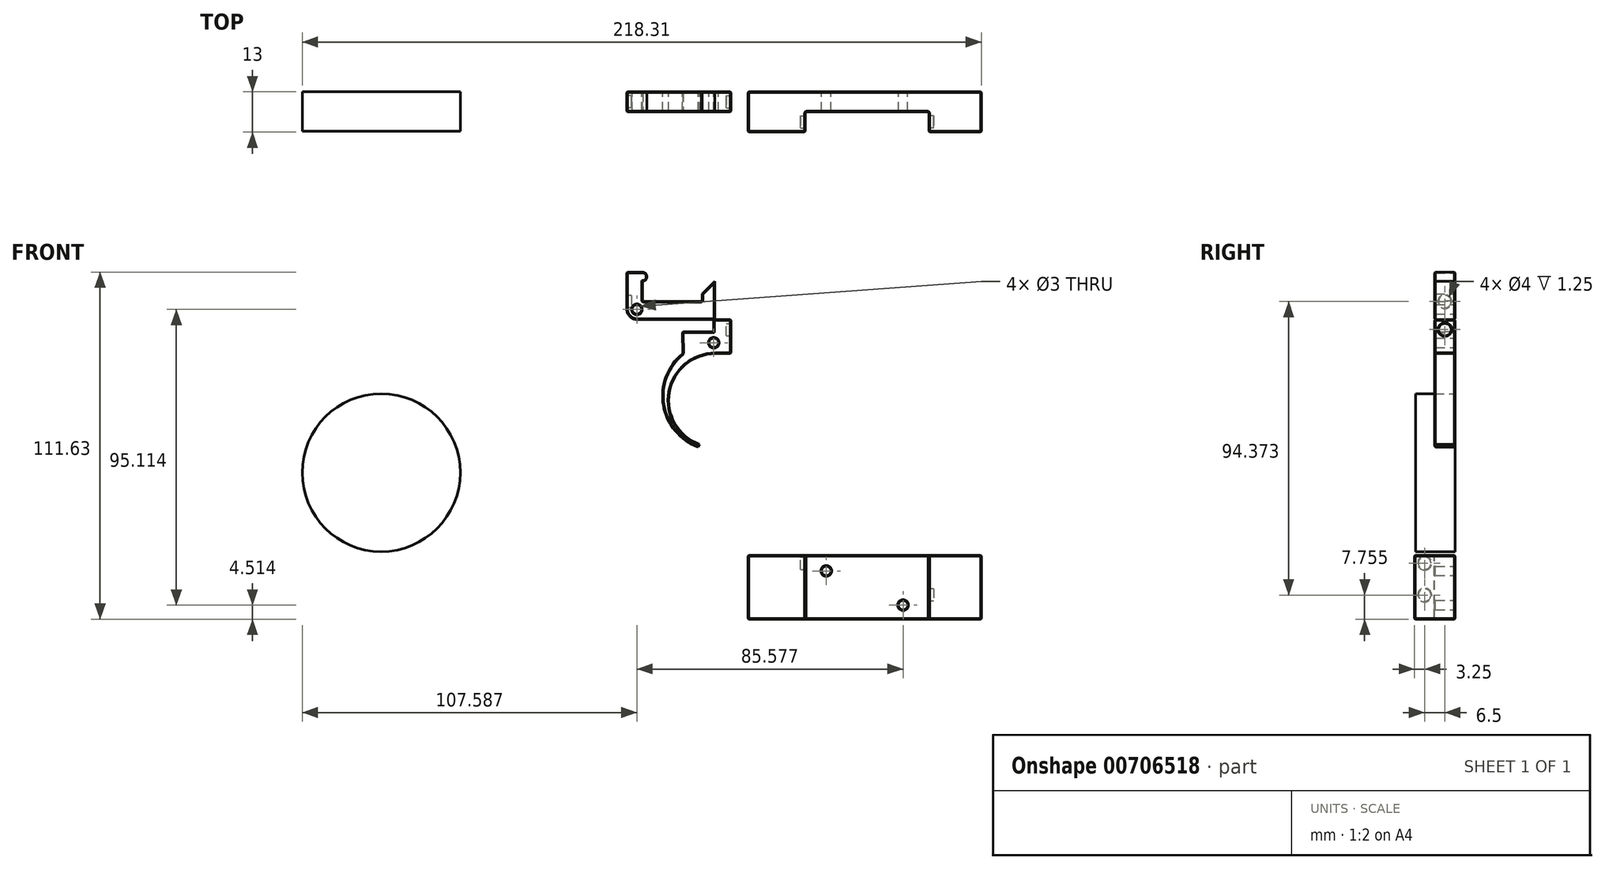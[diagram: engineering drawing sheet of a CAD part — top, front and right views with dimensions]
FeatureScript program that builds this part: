
annotation { "Feature Type Name" : "Feature", "Feature Type Description" : "" }
export const myFeature = defineFeature(function(context is Context, id is Id, definition is map)
    precondition{}
    {
        {
            var Q0;
            Q0=qCreatedBy(makeId("Front.planeOp"),FACE);
            var sketch = newSketch(context, id + "F0", { "sketchPlane" : qUnion([Q0])});
            skArc(sketch, "E0", {"start": v(16.2, 42.27) * mm, "mid": v(1.44, 29.87) * mm, "end": v(11.1, 13.17) * mm});
            skArc(sketch, "E1", {"start": v(5.7, 42.27) * mm, "mid": v(-0.53, 25.78) * mm, "end": v(10.76, 12.23) * mm});
            skLineSegment(sketch, "E2", {"start": v(16.22, 27.27) * mm, "end": v(19.22, 27.27) * mm, "construction": true});
            skLineSegment(sketch, "E3", {"start": v(10.76, 12.23) * mm, "end": v(16.73, 28.68) * mm, "construction": true});
            skLineSegment(sketch, "E4", {"start": v(16.22, 27.27) * mm, "end": v(5.7, 42.27) * mm, "construction": true});
            skLineSegment(sketch, "E5", {"start": v(16.22, 27.27) * mm, "end": v(16.2, 42.27) * mm, "construction": true});
            skLineSegment(sketch, "E6", {"start": v(11.1, 13.17) * mm, "end": v(10.76, 12.23) * mm});
            skLineSegment(sketch, "E7", {"start": v(21.2, 53.28) * mm, "end": v(15.7, 53.28) * mm});
            skLineSegment(sketch, "E8", {"start": v(5.7, 49.27) * mm, "end": v(15.7, 49.28) * mm});
            skLineSegment(sketch, "E9.trimOffspring", {"start": v(15.7, 49.28) * mm, "end": v(15.7, 53.28) * mm});
            skLineSegment(sketch, "E10", {"start": v(5.7, 42.27) * mm, "end": v(5.7, 49.27) * mm});
            skLineSegment(sketch, "E11", {"start": v(21.2, 53.28) * mm, "end": v(21.2, 42.28) * mm});
            skLineSegment(sketch, "E12", {"start": v(-7.25, 59.03) * mm, "end": v(12, 59.03) * mm});
            skLineSegment(sketch, "E13", {"start": v(12, 61.53) * mm, "end": v(16, 65.53) * mm});
            skLineSegment(sketch, "E14", {"start": v(16, 65.53) * mm, "end": v(16, 53.28) * mm});
            skLineSegment(sketch, "E15", {"start": v(16, 53.28) * mm, "end": v(-9, 53.28) * mm});
            skLineSegment(sketch, "E16", {"start": v(-12.25, 56.53) * mm, "end": v(-12.25, 68.53) * mm});
            skLineSegment(sketch, "E17", {"start": v(-12.25, 68.53) * mm, "end": v(-7.25, 68.53) * mm});
            skCircle(sketch, "E18", {"center": v(-9, 56.53) * mm, "radius": 1.5 * mm});
            skCircle(sketch, "E19", {"center": v(15.7, 45.78) * mm, "radius": 1.5 * mm});
            skLineSegment(sketch, "E20", {"start": v(15.7, 49.28) * mm, "end": v(15.7, 45.78) * mm, "construction": true});
            skLineSegment(sketch, "E21", {"start": v(5.7, 45.77) * mm, "end": v(17.2, 45.78) * mm, "construction": true});
            skLineSegment(sketch, "E22", {"start": v(15.7, 49.28) * mm, "end": v(16, 49.28) * mm, "construction": true});
            skLineSegment(sketch, "E23", {"start": v(16, 49.28) * mm, "end": v(16, 53.28) * mm, "construction": true});
            skLineSegment(sketch, "E24", {"start": v(15.7, 45.78) * mm, "end": v(-9, 45.78) * mm, "construction": true});
            skLineSegment(sketch, "E25", {"start": v(-9, 45.78) * mm, "end": v(-9, 56.53) * mm, "construction": true});
            skLineSegment(sketch, "E26", {"start": v(-9, 56.53) * mm, "end": v(-12.25, 56.53) * mm, "construction": true});
            skLineSegment(sketch, "E27", {"start": v(-9, 56.53) * mm, "end": v(-9, 68.53) * mm, "construction": true});
            skArc(sketch, "E28", {"start": v(-7.25, 65.53) * mm, "mid": v(-5.75, 67.03) * mm, "end": v(-7.25, 68.53) * mm});
            skLineSegment(sketch, "E29", {"start": v(-7.25, 65.53) * mm, "end": v(-7.25, 59.03) * mm});
            skLineSegment(sketch, "E30", {"start": v(-7.25, 68.53) * mm, "end": v(-7.25, 67.03) * mm, "construction": true});
            skLineSegment(sketch, "E31", {"start": v(-7.25, 67.03) * mm, "end": v(-7.25, 65.53) * mm, "construction": true});
            skLineSegment(sketch, "E32", {"start": v(-9, 56.53) * mm, "end": v(-9, 53.28) * mm, "construction": true});
            skLineSegment(sketch, "E33", {"start": v(-5.75, 67.03) * mm, "end": v(-12.25, 67.03) * mm, "construction": true});
            skArc(sketch, "E34", {"start": v(-12.25, 56.53) * mm, "mid": v(-11.3, 54.23) * mm, "end": v(-9, 53.28) * mm});
            skLineSegment(sketch, "E35", {"start": v(-9, 56.53) * mm, "end": v(16, 56.53) * mm, "construction": true});
            skLineSegment(sketch, "E36", {"start": v(12, 59.03) * mm, "end": v(12, 61.53) * mm});
            skLineSegment(sketch, "E37", {"start": v(-9, 56.53) * mm, "end": v(-9, 61.53) * mm, "construction": true});
            skLineSegment(sketch, "E38", {"start": v(-9, 61.53) * mm, "end": v(55.4, 61.53) * mm, "construction": true});
            skLineSegment(sketch, "E39.bottom", {"start": v(26.72, -22.6) * mm, "end": v(101.72, -22.6) * mm});
            skLineSegment(sketch, "E39.top", {"start": v(26.72, -43.1) * mm, "end": v(101.72, -43.1) * mm});
            skLineSegment(sketch, "E39.left", {"start": v(26.72, -22.6) * mm, "end": v(26.72, -43.1) * mm});
            skLineSegment(sketch, "E39.right", {"start": v(101.72, -22.6) * mm, "end": v(101.72, -43.1) * mm});
            skCircle(sketch, "E40", {"center": v(51.87, -27.6) * mm, "radius": 1.5 * mm});
            skCircle(sketch, "E41", {"center": v(76.57, -38.59) * mm, "radius": 1.5 * mm});
            skLineSegment(sketch, "E42", {"start": v(51.87, -27.6) * mm, "end": v(76.57, -38.59) * mm, "construction": true});
            skLineSegment(sketch, "E43", {"start": v(64.22, -33.1) * mm, "end": v(64.22, -22.6) * mm, "construction": true});
            skLineSegment(sketch, "E44", {"start": v(21.2, 42.28) * mm, "end": v(16.2, 42.27) * mm});
            skLineSegment(sketch, "E45", {"start": v(12, 61.53) * mm, "end": v(12, 56.53) * mm, "construction": true});
            skCircle(sketch, "E46", {"center": v(-91.2, 4.02) * mm, "radius": 25.4 * mm});
            skSolve(sketch);
        }
        {
            assignVariable(context, id + "F1", {"name" : "SearWidth", "anyValue" : 6.5});
        }
        {
            var Q0;
            Q0=makeQuery(id+"F0.imprint","IMPRINT",FACE,{"disambiguationData":[TD([[makeQuery(id+"F0.imprint","IMPRINT",EDGE,{"derivedFrom":sQuery(id+"F0.wireOp",EDGE,"E12")}),-1.0]])]});
            var Q1;
            Q1=makeQuery(id+"F0.imprint","IMPRINT",FACE,{"disambiguationData":[TD([[makeQuery(id+"F0.imprint","IMPRINT",EDGE,{"derivedFrom":sQuery(id+"F0.wireOp",EDGE,"E0")}),-1.0]])]});
            extrude(context, id + "F2", {"entities" : qUnion([Q0, Q1]), "depth" : (getVariable(context, 'SearWidth')) * mm, "offsetDistance" : 25 * mm});
        }
        {
            var Q0;
            Q0=makeQuery(id+"F0.imprint","IMPRINT",FACE,{"disambiguationData":[TD([[makeQuery(id+"F0.imprint","IMPRINT",EDGE,{"derivedFrom":sQuery(id+"F0.wireOp",EDGE,"E39.bottom")}),-1.0]])]});
            extrude(context, id + "F3", {"entities" : qUnion([Q0]), "depth" : (2 * getVariable(context, 'SearWidth')) * mm, "offsetDistance" : 25 * mm});
        }
        {
            assignVariable(context, id + "F4", {"name" : "TriggerSpringPocketDepth", "anyValue" : 1.5});
        }
        {
            var Q0;
            Q0=makeQuery(id+"F2.opExtrude","SWEPT_FACE",FACE,{"disambiguationData":[OSD([sQuery(id+"F0.wireOp",EDGE,"E16")])]});
            var sketch = newSketch(context, id + "F5", { "sketchPlane" : qUnion([Q0])});
            skCircle(sketch, "E47", {"center": v(3.25, 59.03) * mm, "radius": 2 * mm});
            skSolve(sketch);
        }
        {
            var Q0;
            Q0=makeQuery(id+"F5.imprint","IMPRINT",FACE,{"disambiguationData":[TD([[makeQuery(id+"F5.imprint","IMPRINT",EDGE,{"derivedFrom":sQuery(id+"F5.wireOp",EDGE,"E47")}),1.0]])]});
            extrude(context, id + "F6", {"entities" : qUnion([Q0]), "operationType" : NewBodyOperationType.REMOVE, "oppositeDirection" : true, "depth" : (getVariable(context, 'TriggerSpringPocketDepth')) * mm, "offsetDistance" : 25 * mm});
        }
        {
            var Q0;
            Q0=makeQuery(id+"F2.opExtrude","SWEPT_FACE",FACE,{"disambiguationData":[OSD([sQuery(id+"F0.wireOp",EDGE,"E11")])]});
            var sketch = newSketch(context, id + "F7", { "sketchPlane" : qUnion([Q0])});
            skCircle(sketch, "E48", {"center": v(-3.25, 50.01) * mm, "radius": 2 * mm});
            skSolve(sketch);
        }
        {
            var Q0;
            Q0=makeQuery(id+"F7.imprint","IMPRINT",FACE,{"disambiguationData":[TD([[makeQuery(id+"F7.imprint","IMPRINT",EDGE,{"derivedFrom":sQuery(id+"F7.wireOp",EDGE,"E48")}),1.0]])]});
            extrude(context, id + "F8", {"entities" : qUnion([Q0]), "operationType" : NewBodyOperationType.REMOVE, "oppositeDirection" : true, "depth" : (getVariable(context, 'TriggerSpringPocketDepth')) * mm, "offsetDistance" : 25 * mm});
        }
        {
            var Q0;
            Q0=makeQuery(id+"F3.opExtrude","SWEPT_FACE",FACE,{"disambiguationData":[OSD([sQuery(id+"F0.wireOp",EDGE,"E39.top")])]});
            var sketch = newSketch(context, id + "F9", { "sketchPlane" : qUnion([Q0])});
            skLineSegment(sketch, "E49", {"start": v(45.12, 13) * mm, "end": v(84.87, 13) * mm});
            skLineSegment(sketch, "E50", {"start": v(84.87, 13) * mm, "end": v(84.87, 6.5) * mm});
            skLineSegment(sketch, "E51", {"start": v(84.87, 6.5) * mm, "end": v(45.12, 6.5) * mm});
            skLineSegment(sketch, "E52", {"start": v(45.12, 6.5) * mm, "end": v(45.12, 13) * mm});
            skPoint(sketch, "E53.orphan", {"position": v(64.22, 13) * mm});
            skSolve(sketch);
        }
        {
            var Q0;
            Q0=makeQuery(id+"F9.imprint","IMPRINT",FACE,{"disambiguationData":[TD([[makeQuery(id+"F9.imprint","IMPRINT",EDGE,{"derivedFrom":sQuery(id+"F9.wireOp",EDGE,"E49")}),-1.0]])]});
            extrude(context, id + "F10", {"entities" : qUnion([Q0]), "operationType" : NewBodyOperationType.REMOVE, "endBound" : BoundingType.UP_TO_NEXT, "oppositeDirection" : true, "depth" : 25 * mm, "offsetDistance" : 25 * mm});
        }
        {
            var Q0;
            Q0=makeQuery(id+"F0.imprint","IMPRINT",FACE,{"disambiguationData":[TD([[makeQuery(id+"F0.imprint","IMPRINT",EDGE,{"derivedFrom":sQuery(id+"F0.wireOp",EDGE,"E46")}),1.0]])]});
            extrude(context, id + "F11", {"entities" : qUnion([Q0]), "depth" : 12.7 * mm, "offsetDistance" : 25 * mm});
        }
        {
            var Q0;
            Q0=makeQuery(id+"F10.boolean.opBoolean","COPY",FACE,{"derivedFrom":makeQuery(id+"F10.opExtrude","SWEPT_FACE",FACE,{"disambiguationData":[OSD([sQuery(id+"F9.wireOp",EDGE,"E52")])]})});
            var sketch = newSketch(context, id + "F12", { "sketchPlane" : qUnion([Q0])});
            skLineSegment(sketch, "E54", {"start": v(-9.75, -22.6) * mm, "end": v(-9.75, -25.1) * mm});
            skCircle(sketch, "E55", {"center": v(-9.75, -25.1) * mm, "radius": 2 * mm});
            skSolve(sketch);
        }
        {
            var Q0;
            Q0=makeQuery(id+"F12.imprint","IMPRINT",FACE,{"disambiguationData":[TD([[makeQuery(id+"F12.imprint","IMPRINT",EDGE,{"derivedFrom":sQuery(id+"F12.wireOp",EDGE,"E55")}),1.0]])]});
            extrude(context, id + "F13", {"entities" : qUnion([Q0]), "operationType" : NewBodyOperationType.REMOVE, "oppositeDirection" : true, "depth" : (getVariable(context, 'TriggerSpringPocketDepth')) * mm, "offsetDistance" : 25 * mm});
        }
        {
            var Q0;
            Q0=makeQuery(id+"F10.boolean.opBoolean","COPY",FACE,{"derivedFrom":makeQuery(id+"F10.opExtrude","SWEPT_FACE",FACE,{"disambiguationData":[OSD([sQuery(id+"F9.wireOp",EDGE,"E50")])]})});
            var sketch = newSketch(context, id + "F14", { "sketchPlane" : qUnion([Q0])});
            skLineSegment(sketch, "E56", {"start": v(9.75, -43.1) * mm, "end": v(9.75, -35.35) * mm});
            skCircle(sketch, "E57", {"center": v(9.75, -35.35) * mm, "radius": 2 * mm});
            skSolve(sketch);
        }
        {
            var Q0;
            Q0=makeQuery(id+"F14.imprint","IMPRINT",FACE,{"disambiguationData":[TD([[makeQuery(id+"F14.imprint","IMPRINT",EDGE,{"derivedFrom":sQuery(id+"F14.wireOp",EDGE,"E57")}),1.0]])]});
            extrude(context, id + "F15", {"entities" : qUnion([Q0]), "operationType" : NewBodyOperationType.REMOVE, "oppositeDirection" : true, "depth" : (getVariable(context, 'TriggerSpringPocketDepth')) * mm, "offsetDistance" : 25 * mm});
        }
        {
            var Q0;
            Q0=makeQuery(id+"F2.opExtrude","SWEPT_FACE",FACE,{"disambiguationData":[OSD([sQuery(id+"F0.wireOp",EDGE,"E16")])]});
            var Q1;
            Q1=makeQuery(id+"F2.opExtrude","CAP_FACE",FACE,{"disambiguationData":[OSD([sQuery(id+"F0.wireOp",EDGE,"E12"),sQuery(id+"F0.wireOp",EDGE,"E13"),sQuery(id+"F0.wireOp",EDGE,"E14"),sQuery(id+"F0.wireOp",EDGE,"E15"),sQuery(id+"F0.wireOp",EDGE,"E16"),sQuery(id+"F0.wireOp",EDGE,"E17"),sQuery(id+"F0.wireOp",EDGE,"E18"),sQuery(id+"F0.wireOp",EDGE,"E28"),sQuery(id+"F0.wireOp",EDGE,"E29"),sQuery(id+"F0.wireOp",EDGE,"E34"),sQuery(id+"F0.wireOp",EDGE,"E36")])],"isStart":false});
            var Q2;
            Q2=makeQuery(id+"F2.opExtrude","CAP_FACE",FACE,{"disambiguationData":[OSD([sQuery(id+"F0.wireOp",EDGE,"E12"),sQuery(id+"F0.wireOp",EDGE,"E13"),sQuery(id+"F0.wireOp",EDGE,"E14"),sQuery(id+"F0.wireOp",EDGE,"E15"),sQuery(id+"F0.wireOp",EDGE,"E16"),sQuery(id+"F0.wireOp",EDGE,"E17"),sQuery(id+"F0.wireOp",EDGE,"E18"),sQuery(id+"F0.wireOp",EDGE,"E28"),sQuery(id+"F0.wireOp",EDGE,"E29"),sQuery(id+"F0.wireOp",EDGE,"E34"),sQuery(id+"F0.wireOp",EDGE,"E36")])],"isStart":true});
            var Q3;
            Q3=makeQuery(id+"F2.opExtrude","SWEPT_FACE",FACE,{"disambiguationData":[OSD([sQuery(id+"F0.wireOp",EDGE,"E12")])]});
            var Q4;
            Q4=makeQuery(id+"F2.opExtrude","CAP_FACE",FACE,{"disambiguationData":[OSD([sQuery(id+"F0.wireOp",EDGE,"E0"),sQuery(id+"F0.wireOp",EDGE,"E1"),sQuery(id+"F0.wireOp",EDGE,"E6"),sQuery(id+"F0.wireOp",EDGE,"E7"),sQuery(id+"F0.wireOp",EDGE,"E8"),sQuery(id+"F0.wireOp",EDGE,"E9.trimOffspring"),sQuery(id+"F0.wireOp",EDGE,"E10"),sQuery(id+"F0.wireOp",EDGE,"E11"),sQuery(id+"F0.wireOp",EDGE,"E19"),sQuery(id+"F0.wireOp",EDGE,"E44")])],"isStart":true});
            var Q5;
            Q5=makeQuery(id+"F2.opExtrude","CAP_FACE",FACE,{"disambiguationData":[OSD([sQuery(id+"F0.wireOp",EDGE,"E0"),sQuery(id+"F0.wireOp",EDGE,"E1"),sQuery(id+"F0.wireOp",EDGE,"E6"),sQuery(id+"F0.wireOp",EDGE,"E7"),sQuery(id+"F0.wireOp",EDGE,"E8"),sQuery(id+"F0.wireOp",EDGE,"E9.trimOffspring"),sQuery(id+"F0.wireOp",EDGE,"E10"),sQuery(id+"F0.wireOp",EDGE,"E11"),sQuery(id+"F0.wireOp",EDGE,"E19"),sQuery(id+"F0.wireOp",EDGE,"E44")])],"isStart":false});
            var Q6;
            Q6=makeQuery(id+"F2.opExtrude","SWEPT_FACE",FACE,{"disambiguationData":[OSD([sQuery(id+"F0.wireOp",EDGE,"E10")])]});
            var Q7;
            Q7=makeQuery(id+"F2.opExtrude","SWEPT_FACE",FACE,{"disambiguationData":[OSD([sQuery(id+"F0.wireOp",EDGE,"E11")])]});
            var Q8;
            {var subQ0=sQuery(id+"F0.wireOp",EDGE,"E39.bottom");var subQ1=sQuery(id+"F0.wireOp",EDGE,"E39.top");var subQ2=sQuery(id+"F0.wireOp",EDGE,"E39.left");Q8=makeQuery(id+"F10.boolean.opBoolean","SPLIT",FACE,{"disambiguationData":[TD([makeQuery(id+"F3.opExtrude","SWEPT_FACE",FACE,{"disambiguationData":[OSD([subQ2])]})])],"derivedFrom":makeQuery(id+"F3.opExtrude","CAP_FACE",FACE,{"disambiguationData":[OSD([subQ0,subQ1,subQ2,sQuery(id+"F0.wireOp",EDGE,"E39.right"),sQuery(id+"F0.wireOp",EDGE,"E40"),sQuery(id+"F0.wireOp",EDGE,"E41")])],"isStart":false})});}
            var Q9;
            Q9=makeQuery(id+"F10.boolean.opBoolean","COPY",FACE,{"derivedFrom":makeQuery(id+"F10.opExtrude","SWEPT_FACE",FACE,{"disambiguationData":[OSD([sQuery(id+"F9.wireOp",EDGE,"E52")])]})});
            var Q10;
            Q10=makeQuery(id+"F10.boolean.opBoolean","COPY",FACE,{"derivedFrom":makeQuery(id+"F10.opExtrude","SWEPT_FACE",FACE,{"disambiguationData":[OSD([sQuery(id+"F9.wireOp",EDGE,"E51")])]})});
            var Q11;
            {var subQ0=sQuery(id+"F0.wireOp",EDGE,"E39.bottom");var subQ1=sQuery(id+"F0.wireOp",EDGE,"E39.right");var subQ2=sQuery(id+"F0.wireOp",EDGE,"E39.top");Q11=makeQuery(id+"F10.boolean.opBoolean","SPLIT",FACE,{"disambiguationData":[TD([makeQuery(id+"F3.opExtrude","SWEPT_FACE",FACE,{"disambiguationData":[OSD([subQ1])]})])],"derivedFrom":makeQuery(id+"F3.opExtrude","CAP_FACE",FACE,{"disambiguationData":[OSD([subQ0,subQ2,sQuery(id+"F0.wireOp",EDGE,"E39.left"),subQ1,sQuery(id+"F0.wireOp",EDGE,"E40"),sQuery(id+"F0.wireOp",EDGE,"E41")])],"isStart":false})});}
            var Q12;
            Q12=makeQuery(id+"F3.opExtrude","SWEPT_FACE",FACE,{"disambiguationData":[OSD([sQuery(id+"F0.wireOp",EDGE,"E39.right")])]});
            var Q13;
            Q13=makeQuery(id+"F3.opExtrude","SWEPT_FACE",FACE,{"disambiguationData":[OSD([sQuery(id+"F0.wireOp",EDGE,"E39.bottom")])]});
            var Q14;
            Q14=makeQuery(id+"F3.opExtrude","SWEPT_FACE",FACE,{"disambiguationData":[OSD([sQuery(id+"F0.wireOp",EDGE,"E39.top")])]});
            var Q15;
            Q15=makeQuery(id+"F10.boolean.opBoolean","COPY",FACE,{"derivedFrom":makeQuery(id+"F10.opExtrude","SWEPT_FACE",FACE,{"disambiguationData":[OSD([sQuery(id+"F9.wireOp",EDGE,"E50")])]})});
            var Q16;
            Q16=makeQuery(id+"F3.opExtrude","CAP_FACE",FACE,{"disambiguationData":[OSD([sQuery(id+"F0.wireOp",EDGE,"E39.bottom"),sQuery(id+"F0.wireOp",EDGE,"E39.top"),sQuery(id+"F0.wireOp",EDGE,"E39.left"),sQuery(id+"F0.wireOp",EDGE,"E39.right"),sQuery(id+"F0.wireOp",EDGE,"E40"),sQuery(id+"F0.wireOp",EDGE,"E41")])],"isStart":true});
            var Q17;
            Q17=makeQuery(id+"F3.opExtrude","SWEPT_FACE",FACE,{"disambiguationData":[OSD([sQuery(id+"F0.wireOp",EDGE,"E39.left")])]});
            chamfer(context, id + "F16", {"entities" : qUnion([Q0, Q1, Q2, Q3, Q4, Q5, Q6, Q7, Q8, Q9, Q10, Q11, Q12, Q13, Q14, Q15, Q16, Q17]), "width" : 0.25 * mm, "tangentPropagation" : true});
        }
    });
